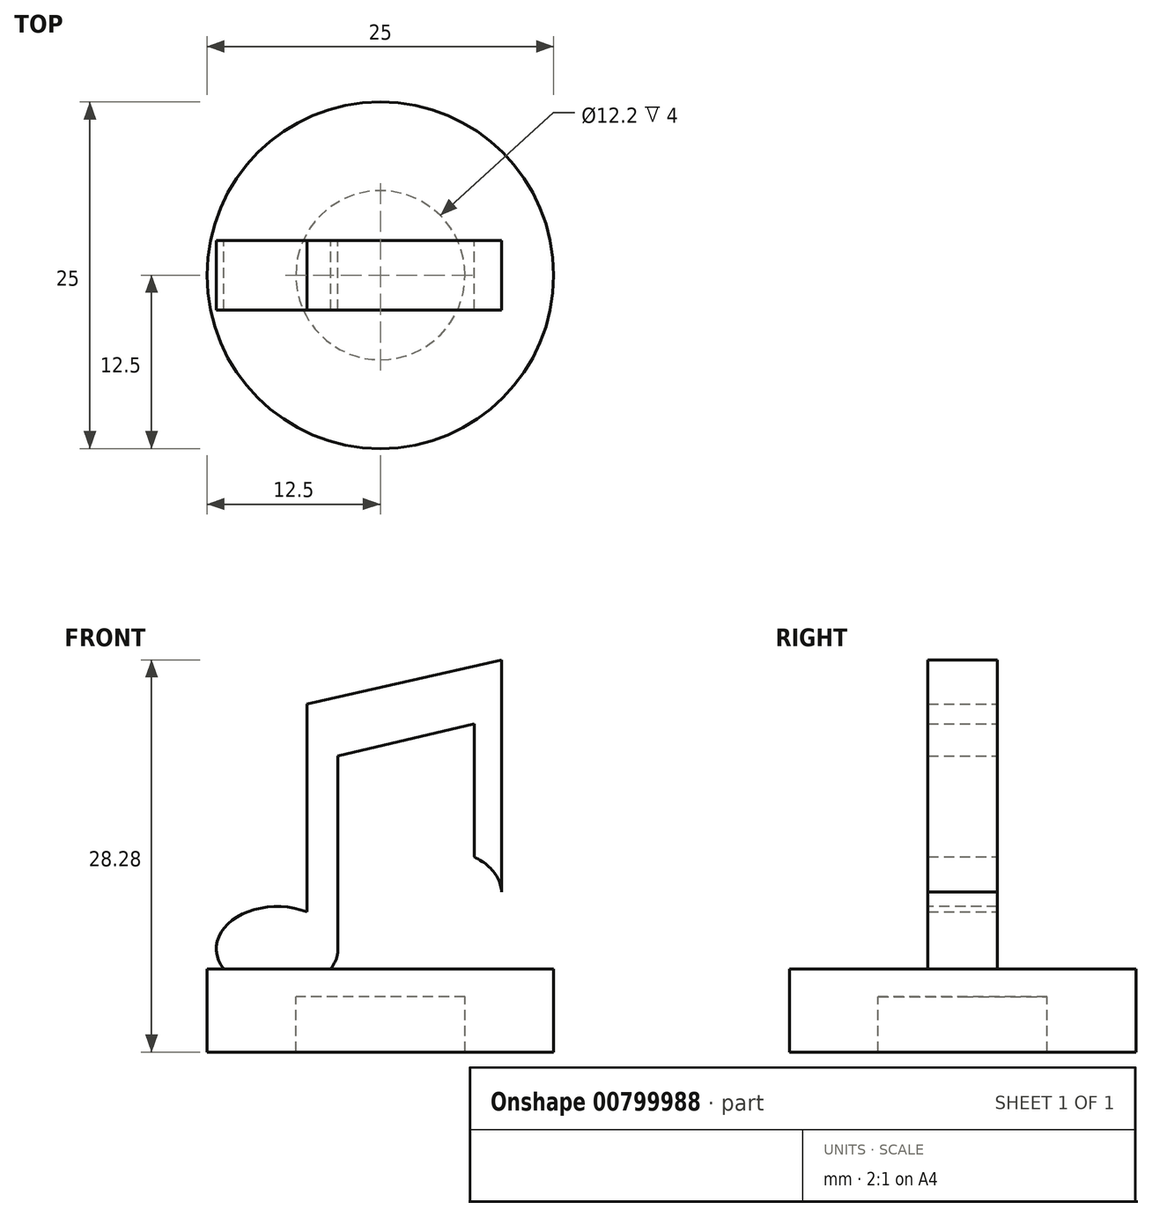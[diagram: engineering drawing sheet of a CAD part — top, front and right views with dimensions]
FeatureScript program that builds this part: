
annotation { "Feature Type Name" : "Feature", "Feature Type Description" : "" }
export const myFeature = defineFeature(function(context is Context, id is Id, definition is map)
    precondition{}
    {
        {
            var Q0;
            Q0=qCreatedBy(makeId("Top.planeOp"),FACE);
            var sketch = newSketch(context, id + "F0", { "sketchPlane" : qUnion([Q0])});
            skCircle(sketch, "E0", {"center": v(0, 0) * mm, "radius": 6.1 * mm});
            skCircle(sketch, "E1", {"center": v(0, 0) * mm, "radius": 12.5 * mm});
            skSolve(sketch);
        }
        {
            var Q0;
            Q0=makeQuery(id+"F0.imprint","IMPRINT",FACE,{"disambiguationData":[TD([[makeQuery(id+"F0.imprint","IMPRINT",EDGE,{"derivedFrom":sQuery(id+"F0.wireOp",EDGE,"E0")}),-1.0]])]});
            extrude(context, id + "F1", {"entities" : qUnion([Q0]), "oppositeDirection" : true, "depth" : 6 * mm, "offsetDistance" : 25 * mm});
        }
        {
            var Q0;
            Q0=makeQuery(id+"F0.imprint","IMPRINT",FACE,{"disambiguationData":[TD([[makeQuery(id+"F0.imprint","IMPRINT",EDGE,{"derivedFrom":sQuery(id+"F0.wireOp",EDGE,"E0")}),1.0]])]});
            extrude(context, id + "F2", {"entities" : qUnion([Q0]), "operationType" : NewBodyOperationType.ADD, "oppositeDirection" : true, "depth" : 2 * mm, "offsetDistance" : 25 * mm});
        }
        {
            var Q0;
            Q0=qCreatedBy(makeId("Front.planeOp"),FACE);
            var sketch = newSketch(context, id + "F3", { "sketchPlane" : qUnion([Q0])});
            skLineSegment(sketch, "E2", {"start": v(-5.3, 19.1) * mm, "end": v(8.75, 22.28) * mm});
            skLineSegment(sketch, "E3", {"start": v(8.75, 22.28) * mm, "end": v(8.75, 5.34) * mm});
            skLineSegment(sketch, "E4", {"start": v(-5.3, 19.1) * mm, "end": v(-5.3, 4.1) * mm});
            skLineSegment(sketch, "E5", {"start": v(-3.06, 1.44) * mm, "end": v(-3.06, 15.37) * mm});
            skLineSegment(sketch, "E6", {"start": v(-3.06, 15.37) * mm, "end": v(6.76, 17.67) * mm});
            skLineSegment(sketch, "E7", {"start": v(6.76, 17.67) * mm, "end": v(6.76, 8.08) * mm});
            skEllipse(sketch, "E8", {"center": v(-7.44, 1.44) * mm, "majorRadius": 4.39 * mm, "minorRadius": 3.05 * mm, "majorAxis": v(1, 0)});
            skEllipse(sketch, "E9", {"center": v(4.46, 5.55) * mm, "majorRadius": 4.3 * mm, "minorRadius": 3.06 * mm, "majorAxis": v(1, -0.05)});
            skSolve(sketch);
        }
        {
            var Q0;
            {var subQ0=sQuery(id+"F3.wireOp",EDGE,"E9");var subQ1=sQuery(id+"F3.wireOp",EDGE,"E3");var subQ2=makeQuery(id+"F3.imprint","INTERSECT",VERTEX,{"disambiguationData":[OD(0.0)],"derivedFrom":[subQ1,subQ0]});Q0=makeQuery(id+"F3.imprint","IMPRINT",FACE,{"disambiguationData":[TD([[makeQuery(id+"F3.imprint","IMPRINT",EDGE,{"disambiguationData":[TD([[subQ2,1.0]])],"derivedFrom":subQ1}),1.0]])]});}
            var Q1;
            {var subQ0=sQuery(id+"F3.wireOp",EDGE,"E8");var subQ1=makeQuery(id+"F3.imprint","INTERSECT",VERTEX,{"derivedFrom":[sQuery(id+"F3.wireOp",EDGE,"E4"),subQ0]});Q1=makeQuery(id+"F3.imprint","IMPRINT",FACE,{"disambiguationData":[TD([[makeQuery(id+"F3.imprint","IMPRINT",EDGE,{"disambiguationData":[TD([[subQ1,1.0]])],"derivedFrom":subQ0}),1.0]])]});}
            var Q2;
            {var subQ0=sQuery(id+"F3.wireOp",EDGE,"E9");var subQ1=sQuery(id+"F3.wireOp",EDGE,"E3");var subQ2=makeQuery(id+"F3.imprint","INTERSECT",VERTEX,{"disambiguationData":[OD(0.0)],"derivedFrom":[subQ1,subQ0]});Q2=makeQuery(id+"F3.imprint","IMPRINT",FACE,{"disambiguationData":[TD([[makeQuery(id+"F3.imprint","IMPRINT",EDGE,{"disambiguationData":[TD([[subQ2,1.0]])],"derivedFrom":subQ1}),-1.0]])]});}
            var Q3;
            {var subQ3=sQuery(id+"F3.wireOp",EDGE,"E2");Q3=makeQuery(id+"F3.imprint","IMPRINT",FACE,{"disambiguationData":[TD([[makeQuery(id+"F3.imprint","IMPRINT",EDGE,{"derivedFrom":subQ3}),-1.0]])]});}
            extrude(context, id + "F4", {"entities" : qUnion([Q0, Q1, Q2, Q3]), "operationType" : NewBodyOperationType.ADD, "endBound" : BoundingType.SYMMETRIC, "depth" : 5 * mm, "offsetDistance" : 25 * mm});
        }
    });
